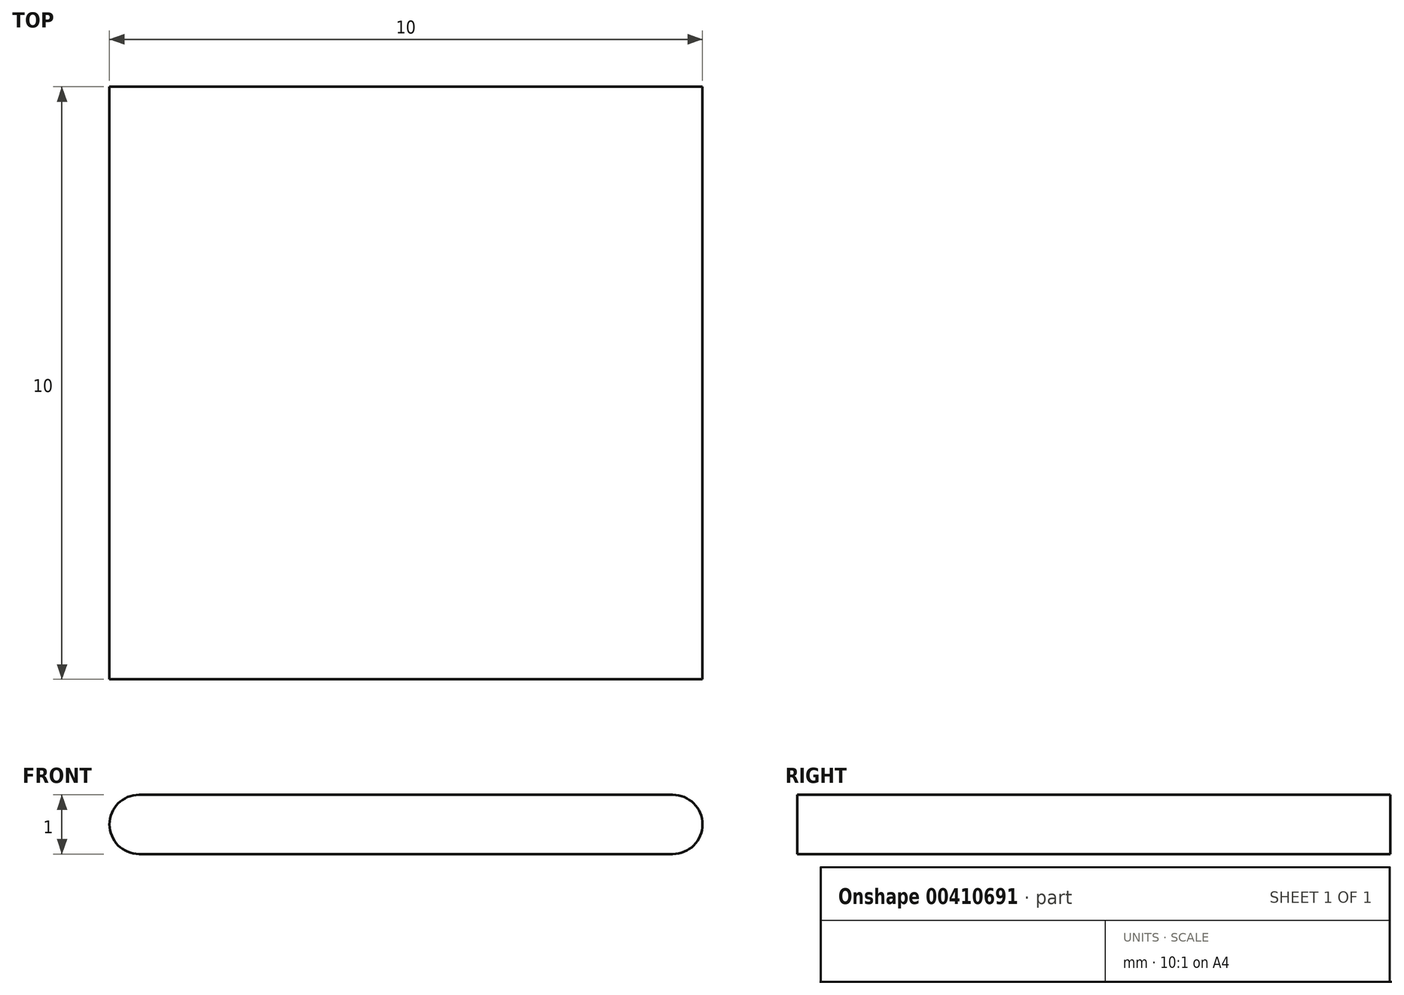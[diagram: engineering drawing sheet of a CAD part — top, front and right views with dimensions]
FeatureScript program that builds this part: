
annotation { "Feature Type Name" : "Feature", "Feature Type Description" : "" }
export const myFeature = defineFeature(function(context is Context, id is Id, definition is map)
    precondition{}
    {
        {
            var Q0;
            Q0=qCreatedBy(makeId("Front.planeOp"),FACE);
            var sketch = newSketch(context, id + "F0", { "sketchPlane" : qUnion([Q0])});
            skLineSegment(sketch, "E0.bottom", {"start": v(4.5, 0.5) * mm, "end": v(-4.5, 0.5) * mm});
            skLineSegment(sketch, "E0.top", {"start": v(4.5, -0.5) * mm, "end": v(-4.5, -0.5) * mm});
            skPoint(sketch, "E0.middle", {"position": v(0, 0) * mm});
            skArc(sketch, "E1", {"start": v(4.5, -0.5) * mm, "mid": v(5, 0) * mm, "end": v(4.5, 0.5) * mm});
            skArc(sketch, "E2", {"start": v(-4.5, 0.5) * mm, "mid": v(-5, 0) * mm, "end": v(-4.5, -0.5) * mm});
            skSolve(sketch);
        }
        {
            var Q0;
            Q0=makeQuery(id+"F0.imprint","IMPRINT",FACE,{"disambiguationData":[TD([[makeQuery(id+"F0.imprint","IMPRINT",EDGE,{"derivedFrom":sQuery(id+"F0.wireOp",EDGE,"E0.bottom")}),1.0]])]});
            extrude(context, id + "F1", {"entities" : qUnion([Q0]), "endBound" : BoundingType.SYMMETRIC, "depth" : 10 * mm});
        }
    });
